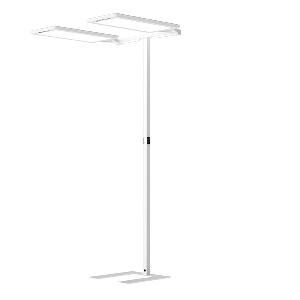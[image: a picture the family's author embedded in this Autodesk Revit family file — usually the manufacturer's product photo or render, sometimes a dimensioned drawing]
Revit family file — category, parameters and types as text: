
# Revit family: yara_doubleu_-_yus_2_8000_840_r_ws_cee_00_c_114268000-00815000_3163
name_source: partatom
category: Lighting Fixtures
units: mm (PartAtom-declared; Revit-internal decimal feet)

## family parameters
Cut with Voids When Loaded = No
Host = Face
Light Source = No
Part Type = Normal
Room Calculation Point = No
Round Connector Dimension = Use Diameter
Shared = No

## types (1)
- YARA.doubleU - YUS 2/8000/840/R/WS/CEE/00/C (1 x LED, 8000 lm, 4000K)
    Apparent Load = 112 VA
    Approval mark = CE
    CIE Flux Codes = 58 87 97 13 100
    Color Rendering = 80-89
    Color Temperature = 4000K
    Control Gear = Electronic ballast
    Default Elevation = 1800 mm
    Description = YUS 2/8000/840/R/WS/CEE/00/C|Free-standing luminaire|light source: LED Cold white   |work equipment: Electronic ballast DALI|power factor: approx. 0,966|luminous flux: 16000 lm|light distribution: Direct/indirect|direct ratio: approx. 13 %|color rendering index (CRI): >= 80|chromaticity tolerance:  3 SDCM|technology: Presence and daylight sensor control (PIR)|operation: Wireless switch|luminaire body|material: Aluminium/plastic|surface: Powder coatet|colour: White|lamp cover: Acrylic (PMMA)|tubular section|material: Steel tube|surface: Powder-coated|Form: Tubular section upright|colour of tubular section: White|luminaire base|Form: C-form flat|weight (net): approx. 26.0 kg|mains lead: 3.00 m Mains plug CEE 7/VII|Fastening: Floor standing base|glare control: Conical prismatic screen|unified glare rating(4H 8H): <=  16|special features: App control, Asymmetric radiation, Direct and indirect lighting component with edge light and light guidetechnology for a homogeneous light exit, Flicker-free, Magnetic control panel, freely positionable, PIR movement and daylight sensor, TALK Bluetooth|Approval mark: VDE - ENEC|
    Frequency = 50 Hz, 60 Hz
    Height = 24 mm  [stored 0.0787402 ft]
    Lamp = 1 x LED
    Lamp Light Flux = 8000 lm
    Lamp count = 1
    Length = 690 mm
    Luminous efficacy = 143 lm/W
    Manufacturer = Waldmann
    ModVariant = No
    Model = 114268000-00815000
    Mounting Place = Floor
    Mounting Type = Freestanding
    Number of Poles = 1
    OnlyDefault = Yes
    Power Factor = 1
    Product Name = YARA.doubleU - YUS 2/8000/840/R/WS/CEE/00/C
    Product group = Free standing luminaire
    ProductGroupID = 13
    Protection Class = Protection class I
    Protection Degree = IP 20
    RLX_Detail_Level = 1
    RlxData = <blob elided: 67081 chars, md5=222454b4>
    Socket = socket
    Standby Power = 0 W
    System Light Flux = 16000 lm
    System Power = 112 W
    Type Comments = Product without accessories
    Type Image = yus-r-ws-c.jpg
    URL = http://relux.com
    VarID = ---
    Voltage = 230 V
    Voltage Range = 220-240 V
    Weight = 0.00 kg
    Width = 358 mm

note: [stored X ft] marks values corroborated as IEEE doubles in the binary element streams (Revit-internal decimal feet)

## geometry (parser evidence)
native form markers: Blend x4, Sweep x17
no freeform markers — native parametric forms only
